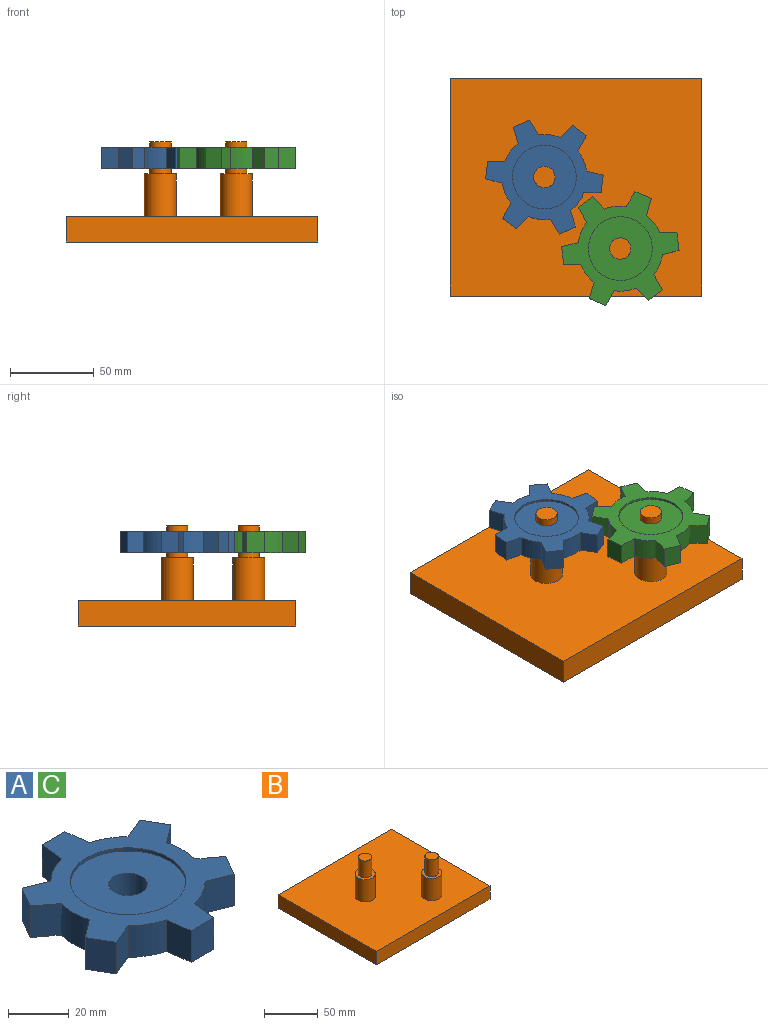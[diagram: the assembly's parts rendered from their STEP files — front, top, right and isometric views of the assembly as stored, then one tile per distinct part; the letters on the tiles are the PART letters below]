
ASSEMBLY  parts=3 mates=2
PART A: 31 faces, bbox 65.4x69.4x12.7 mm
  f0: cylinder r=25.4mm len=12.7mm, axis (0,0,-1), area 168.9mm2, adj f6,f7,f10,f24
  f1: cylinder r=25.4mm len=13.15mm, axis (0,0,-1), area 168.9mm2, adj f6,f7,f13,f25
  f2: cylinder r=25.4mm len=12.7mm, axis (0,0,-1), area 168.9mm2, adj f6,f7,f12,f16
  f3: cylinder r=25.4mm len=12.7mm, axis (0,0,-1), area 168.9mm2, adj f6,f7,f15,f19
  f4: cylinder r=25.4mm len=13.15mm, axis (0,0,-1), area 168.9mm2, adj f6,f7,f18,f21
  f5: cylinder r=25.4mm len=12.7mm, axis (0,0,-1), area 168.9mm2, adj f6,f7,f9,f22
  f6: plane 69.39x65.4mm, normal (0,0,1), area 1565.1mm2, adj f0,f1,f2,f3,f4,f5,f8,f9
  f7: plane 69.39x65.4mm, normal (0,0,-1), area 1565.1mm2, adj f0,f1,f2,f3,f4,f5,f8,f9
  f8: plane 12.7x10.61mm, normal (0,1,0), area 134.7mm2, adj f6,f7,f9,f10
  f9: plane 12.7x10.16mm, normal (-0.99,0.12,0), area 130mm2, adj f5,f6,f7,f8
  f10: plane 12.7x10.16mm, normal (0.99,0.12,0), area 130mm2, adj f0,f6,f7,f8
  f11: plane 12.7x9.19mm, normal (0.87,-0.5,0), area 134.7mm2, adj f6,f7,f12,f13
  f12: plane 12.7x9.43mm, normal (-0.39,-0.92,0), area 130mm2, adj f2,f6,f7,f11
  f13: plane 12.7x8.16mm, normal (0.6,0.8,0), area 130mm2, adj f1,f6,f7,f11
  f14: plane 12.7x10.61mm, normal (0,-1,0), area 134.7mm2, adj f6,f7,f15,f16
  f15: plane 12.7x10.16mm, normal (-0.99,-0.12,0), area 130mm2, adj f3,f6,f7,f14
  f16: plane 12.7x10.16mm, normal (0.99,-0.12,0), area 130mm2, adj f2,f6,f7,f14
  f17: plane 12.7x9.19mm, normal (-0.87,-0.5,0), area 134.7mm2, adj f6,f7,f18,f19
  f18: plane 12.7x8.16mm, normal (-0.6,0.8,0), area 130mm2, adj f4,f6,f7,f17
  f19: plane 12.7x9.43mm, normal (0.39,-0.92,0), area 130mm2, adj f3,f6,f7,f17
  f20: plane 12.7x9.19mm, normal (-0.87,0.5,0), area 134.7mm2, adj f6,f7,f21,f22
  f21: plane 12.7x8.16mm, normal (-0.6,-0.8,0), area 130mm2, adj f4,f6,f7,f20
  f22: plane 12.7x9.43mm, normal (0.39,0.92,0), area 130mm2, adj f5,f6,f7,f20
  f23: plane 12.7x9.19mm, normal (0.87,0.5,0), area 134.7mm2, adj f6,f7,f24,f25
  f24: plane 12.7x9.43mm, normal (-0.39,0.92,0), area 130mm2, adj f0,f6,f7,f23
  f25: plane 12.7x8.16mm, normal (0.6,-0.8,0), area 130mm2, adj f1,f6,f7,f23
  f26: cylinder r=19.05mm len=38.1mm, axis (0,0,1), area 152mm2, adj f6,f27
  f27: plane 38.1x38.1mm, normal (0,0,1), area 1013.4mm2, adj f26,f30
  f28: cylinder r=19.05mm len=38.1mm, axis (0,0,-1), area 152mm2, adj f7,f29
  f29: plane 38.1x38.1mm, normal (0,0,-1), area 1013.4mm2, adj f28,f30
  f30: cylinder r=6.35mm len=12.7mm, axis (0,0,1), area 405.4mm2, adj f27,f29
PART B: 14 faces, bbox 150.3x129.8x59.7 mm
  f0: plane 129.85x15.24mm, normal (-1,0,0), area 1978.9mm2, adj f1,f2,f4,f13
  f1: plane 150.33x129.85mm, normal (0,0,1), area 18949.5mm2, adj f0,f3,f4,f5,f7,f13
  f2: plane 150.33x129.85mm, normal (0,0,-1), area 19519.5mm2, adj f0,f3,f4,f13
  f3: plane 129.85x15.24mm, normal (1,0,0), area 1978.9mm2, adj f1,f2,f4,f13
  f4: plane 150.33x15.24mm, normal (0,1,0), area 2291mm2, adj f0,f1,f2,f3
  f5: cylinder r=9.53mm len=25.4mm, axis (0,0,-1), area 1520.1mm2, adj f1,f6
  f6: plane 19.05x19.05mm, normal (0,0,1), area 158.3mm2, adj f5,f11
  f7: cylinder r=9.53mm len=25.4mm, axis (0,0,-1), area 1520.1mm2, adj f1,f8
  f8: plane 19.05x19.05mm, normal (0,0,1), area 158.3mm2, adj f7,f9
  f9: cylinder r=6.35mm len=19.05mm, axis (0,0,-1), area 760.1mm2, adj f8,f10
  f10: plane 12.7x12.7mm, normal (0,0,1), area 126.7mm2, adj f9
  f11: cylinder r=6.35mm len=19.05mm, axis (0,0,-1), area 760.1mm2, adj f6,f12
  f12: plane 12.7x12.7mm, normal (0,0,1), area 126.7mm2, adj f11
  f13: plane 150.33x15.24mm, normal (0,-1,0), area 2291mm2, adj f0,f1,f2,f3
PART C: same geometry as A
PLACE A rot(axis=(0,0,1),83.1deg) t=(-76.29,56.99,48.59)mm
PLACE B t=(-30.99,14.32,-1.58)mm fixed
PLACE C rot(axis=(0,0,-1),83.1deg) t=(-30.99,14.32,48.59)mm
MATE revolute A.f0 <-> B.f7  axis (0,0,1) through (-76.29,56.99,48.59)mm
MATE revolute C.f0 <-> B.f5  axis (0,0,1) through (-30.99,14.32,48.59)mm
